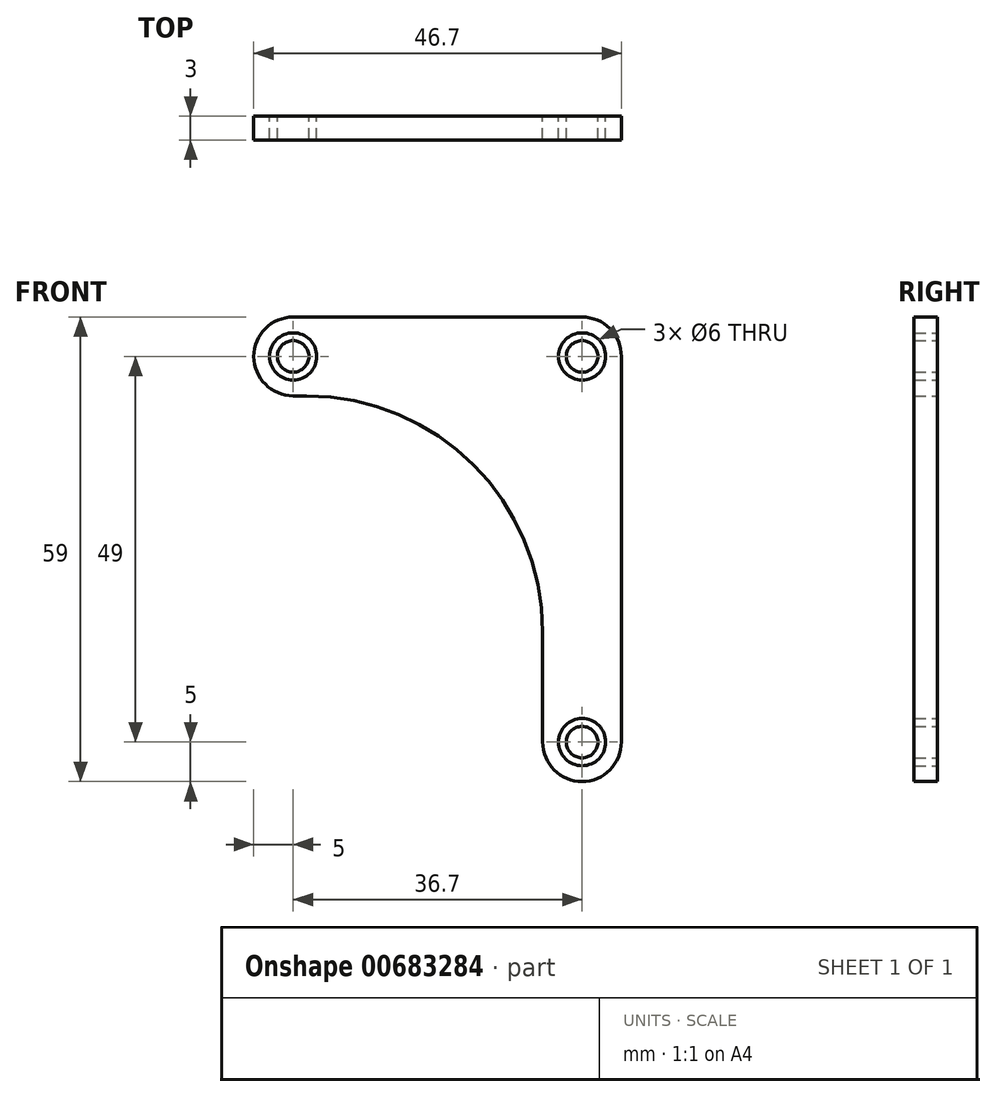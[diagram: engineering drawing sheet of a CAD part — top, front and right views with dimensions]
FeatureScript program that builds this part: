
annotation { "Feature Type Name" : "Feature", "Feature Type Description" : "" }
export const myFeature = defineFeature(function(context is Context, id is Id, definition is map)
    precondition{}
    {
        {
            var Q0;
            Q0=qCreatedBy(makeId("Front.planeOp"),FACE);
            var sketch = newSketch(context, id + "F0", { "sketchPlane" : qUnion([Q0])});
            skArc(sketch, "E0", {"start": v(-36.7, 5) * mm, "mid": v(-41.7, 0) * mm, "end": v(-36.7, -5) * mm});
            skArc(sketch, "E1", {"start": v(5, 0) * mm, "mid": v(3.54, 3.54) * mm, "end": v(0, 5) * mm});
            skArc(sketch, "E2", {"start": v(-5, -49) * mm, "mid": v(0, -54) * mm, "end": v(5, -49) * mm});
            skCircle(sketch, "E3", {"center": v(-36.7, 0) * mm, "radius": 3 * mm});
            skCircle(sketch, "E4", {"center": v(-36.7, 0) * mm, "radius": 2 * mm});
            skCircle(sketch, "E5", {"center": v(0, 0) * mm, "radius": 3 * mm});
            skCircle(sketch, "E6", {"center": v(0, 0) * mm, "radius": 2 * mm});
            skCircle(sketch, "E7", {"center": v(0, -49) * mm, "radius": 3 * mm});
            skCircle(sketch, "E8", {"center": v(0, -49) * mm, "radius": 2 * mm});
            skLineSegment(sketch, "E9", {"start": v(-36.7, 5) * mm, "end": v(0, 5) * mm});
            skLineSegment(sketch, "E10", {"start": v(-36.7, -5) * mm, "end": v(-35, -5) * mm});
            skLineSegment(sketch, "E11", {"start": v(-5, -35) * mm, "end": v(-5, -49) * mm});
            skLineSegment(sketch, "E12", {"start": v(5, 0) * mm, "end": v(5, -49) * mm});
            skPoint(sketch, "E13.visualSharp", {"position": v(-5, -5) * mm});
            skArc(sketch, "E13.filletArc", {"start": v(-5, -35) * mm, "mid": v(-13.79, -13.79) * mm, "end": v(-35, -5) * mm});
            skSolve(sketch);
        }
        {
            var Q0;
            Q0=makeQuery(id+"F0.imprint","IMPRINT",FACE,{"disambiguationData":[TD([[makeQuery(id+"F0.imprint","IMPRINT",EDGE,{"derivedFrom":sQuery(id+"F0.wireOp",EDGE,"E0")}),1.0]])]});
            var Q1;
            Q1=makeQuery(id+"F0.imprint","IMPRINT",FACE,{"disambiguationData":[TD([[makeQuery(id+"F0.imprint","IMPRINT",EDGE,{"derivedFrom":sQuery(id+"F0.wireOp",EDGE,"E4")}),1.0]])]});
            var Q2;
            Q2=makeQuery(id+"F0.imprint","IMPRINT",FACE,{"disambiguationData":[TD([[makeQuery(id+"F0.imprint","IMPRINT",EDGE,{"derivedFrom":sQuery(id+"F0.wireOp",EDGE,"E6")}),1.0]])]});
            var Q3;
            Q3=makeQuery(id+"F0.imprint","IMPRINT",FACE,{"disambiguationData":[TD([[makeQuery(id+"F0.imprint","IMPRINT",EDGE,{"derivedFrom":sQuery(id+"F0.wireOp",EDGE,"E8")}),1.0]])]});
            extrude(context, id + "F1", {"entities" : qUnion([Q0, Q1, Q2, Q3]), "depth" : 3 * mm, "offsetDistance" : 25 * mm});
        }
    });
